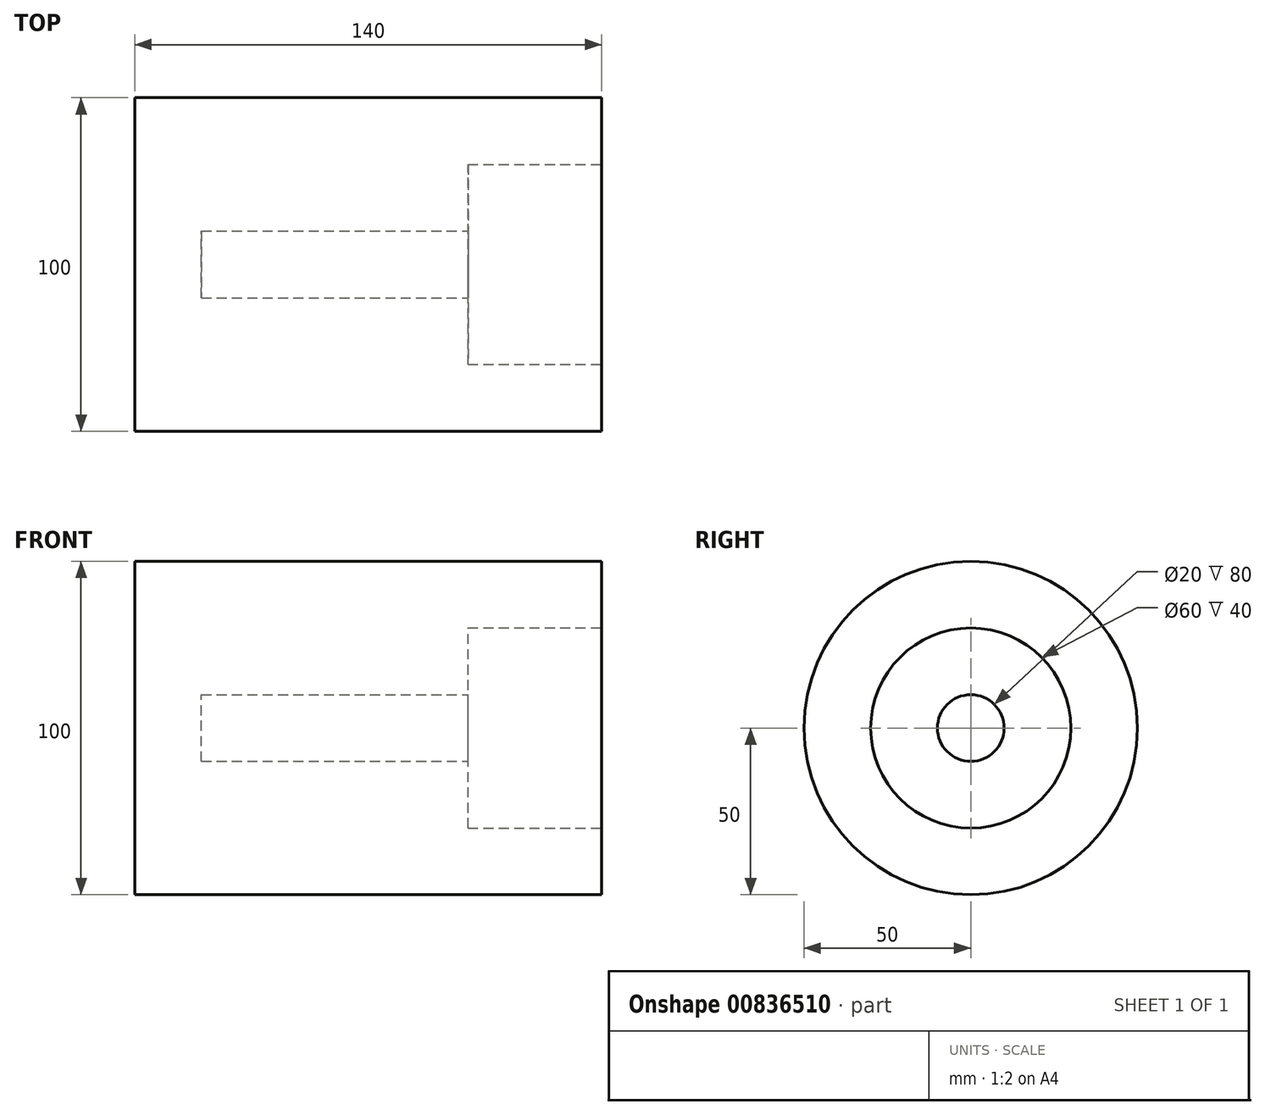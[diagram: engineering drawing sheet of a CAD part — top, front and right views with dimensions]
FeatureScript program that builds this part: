
annotation { "Feature Type Name" : "Feature", "Feature Type Description" : "" }
export const myFeature = defineFeature(function(context is Context, id is Id, definition is map)
    precondition{}
    {
        {
            var Q0;
            Q0=qCreatedBy(makeId("Front.planeOp"),FACE);
            var sketch = newSketch(context, id + "F0", { "sketchPlane" : qUnion([Q0])});
            skLineSegment(sketch, "E0", {"start": v(-70, 0) * mm, "end": v(-70, 50) * mm});
            skLineSegment(sketch, "E1", {"start": v(-70, 50) * mm, "end": v(70, 50) * mm});
            skLineSegment(sketch, "E2", {"start": v(70, 50) * mm, "end": v(70, 30) * mm});
            skLineSegment(sketch, "E3", {"start": v(70, 30) * mm, "end": v(30, 30) * mm});
            skLineSegment(sketch, "E4", {"start": v(30, 30) * mm, "end": v(30, 10) * mm});
            skLineSegment(sketch, "E5", {"start": v(30, 10) * mm, "end": v(-50, 10) * mm});
            skLineSegment(sketch, "E6", {"start": v(-50, 10) * mm, "end": v(-50, 0) * mm});
            skLineSegment(sketch, "E7", {"start": v(-50, 0) * mm, "end": v(-70, 0) * mm});
            skSolve(sketch);
        }
        {
            var Q0;
            Q0=makeQuery(id+"F0.imprint","IMPRINT",FACE,{"disambiguationData":[TD([[makeQuery(id+"F0.imprint","IMPRINT",EDGE,{"derivedFrom":sQuery(id+"F0.wireOp",EDGE,"E0")}),-1.0]])]});
            var Q1;
            Q1=sQuery(id+"F0.wireOp",EDGE,"E7");
            revolve(context, id + "F1", {"surfaceOperationType" : NewSurfaceOperationType.NEW, "entities" : qUnion([Q0]), "axis" : qUnion([Q1]), "revolveType" : RevolveType.FULL});
        }
    });
